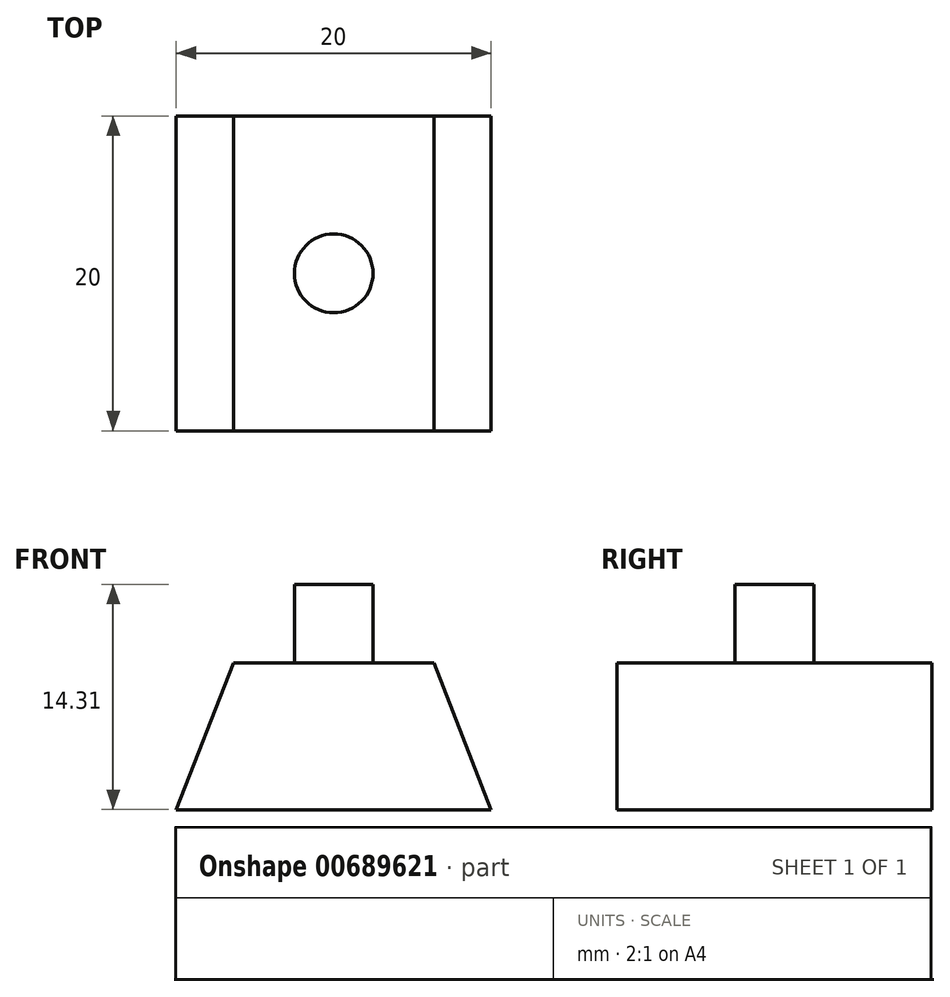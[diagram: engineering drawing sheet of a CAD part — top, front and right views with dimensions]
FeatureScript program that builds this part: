
annotation { "Feature Type Name" : "Feature", "Feature Type Description" : "" }
export const myFeature = defineFeature(function(context is Context, id is Id, definition is map)
    precondition{}
    {
        {
            var Q0;
            Q0=qCreatedBy(makeId("Front.planeOp"),FACE);
            var sketch = newSketch(context, id + "F0", { "sketchPlane" : qUnion([Q0])});
            skLineSegment(sketch, "E0", {"start": v(0, 0) * mm, "end": v(-6.36, 0) * mm});
            skLineSegment(sketch, "E1", {"start": v(0, 0) * mm, "end": v(6.36, 0) * mm});
            skLineSegment(sketch, "E2", {"start": v(0, -9.31) * mm, "end": v(-10, -9.31) * mm});
            skLineSegment(sketch, "E3", {"start": v(0, -9.31) * mm, "end": v(10, -9.31) * mm});
            skLineSegment(sketch, "E4", {"start": v(-6.36, 0) * mm, "end": v(-10, -9.31) * mm});
            skLineSegment(sketch, "E5", {"start": v(6.36, 0) * mm, "end": v(10, -9.31) * mm});
            skSolve(sketch);
        }
        {
            var Q0;
            Q0=makeQuery(id+"F0.imprint","IMPRINT",FACE,{"disambiguationData":[TD([[makeQuery(id+"F0.imprint","IMPRINT",EDGE,{"derivedFrom":sQuery(id+"F0.wireOp",EDGE,"E0")}),1.0]])]});
            extrude(context, id + "F1", {"entities" : qUnion([Q0]), "depth" : 20 * mm, "offsetDistance" : 25 * mm});
        }
        {
            var Q0;
            Q0=makeQuery(id+"F1.opExtrude","SWEPT_FACE",FACE,{"disambiguationData":[OSD([sQuery(id+"F0.wireOp",EDGE,"E0"),sQuery(id+"F0.wireOp",EDGE,"E1")])]});
            var sketch = newSketch(context, id + "F2", { "sketchPlane" : qUnion([Q0])});
            skCircle(sketch, "E6", {"center": v(0, -10) * mm, "radius": 2.5 * mm});
            skSolve(sketch);
        }
        {
            var Q0;
            Q0=makeQuery(id+"F2.imprint","IMPRINT",FACE,{"disambiguationData":[TD([[makeQuery(id+"F2.imprint","IMPRINT",EDGE,{"derivedFrom":sQuery(id+"F2.wireOp",EDGE,"E6")}),1.0]])]});
            var Q1;
            Q1=sQuery(id+"F2.wireOp",EDGE,"E6");
            extrude(context, id + "F3", {"entities" : qUnion([Q0]), "operationType" : NewBodyOperationType.ADD, "surfaceEntities" : qUnion([Q1]), "depth" : 5 * mm, "offsetDistance" : 25 * mm});
        }
    });
